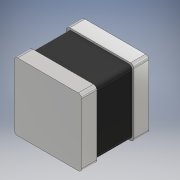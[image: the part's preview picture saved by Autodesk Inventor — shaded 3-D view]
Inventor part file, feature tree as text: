
AUTODESK INVENTOR PART (.ipt)
format: ipt  version: 2017 (Build 210142000, 142)  size: 173,056 bytes
history: native  units: mm
features: extrude x5, sketch x5, fillet x1
ambient origin geometry x8: Origin, YZ Plane, XZ Plane, XY Plane, X Axis, Y Axis, Z Axis, Center Point
bodies: Solide1 (feature_tree)
feature tree (11):
  extrude  "Extrusion1"  Depth=40.0mm
  extrude  "Extrusion2"  Depth=40.0mm
  extrude  "Extrusion3"  Depth=9.0mm TaperAngle=0.0deg
  fillet  "Congé1"  Radius=1.0mm
  extrude  "Extrusion4"  Depth=1.0mm
  extrude  "Extrusion5"  Depth=1.0mm
  sketch  "Esquisse1"
  sketch  "Esquisse2"
  sketch  "Esquisse3"
  sketch  "Esquisse4"
  sketch  "Esquisse5"
